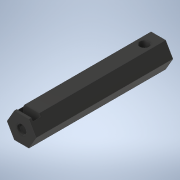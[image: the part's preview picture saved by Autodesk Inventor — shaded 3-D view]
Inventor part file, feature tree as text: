
AUTODESK INVENTOR PART (.ipt)
format: ipt  version: 2020.4 (Build 244396000, 396)  size: 229,376 bytes
history: native  units: mm
features: extrude x11, sketch x11, projected_geometry x6, plane x1, mirror x1
ambient origin geometry x8: Origin, YZ Plane, XZ Plane, XY Plane, X Axis, Y Axis, Z Axis, Center Point
bodies: Solid1 (feature_tree)
feature tree (30):
  extrude  "Extrusion1"  Depth=44.0mm TaperAngle=0.0deg
  extrude  "Extrusion2"  Depth=5.6mm
  extrude  "Extrusion3"  Depth=3.0mm
  plane  "Work Plane1"
  mirror  "Mirror1"
  extrude  "Extrusion4"  TaperAngle=0.0deg  [1 undecoded]
  extrude  "Extrusion5"  TaperAngle=120.0deg  [1 undecoded]
  extrude  "Extrusion6"  Depth=9.5mm TaperAngle=0.0deg
  extrude  "Extrusion8"  Depth=5.6mm
  extrude  "Extrusion9"  Depth=6.0mm TaperAngle=0.0deg
  extrude  "Extrusion10"  TaperAngle=120.0deg  [1 undecoded]
  extrude  "Extrusion11"  Depth=1.9345mm
  extrude  "Extrusion12"  Depth=2.5mm
  sketch  "Sketch1"  dims[d0=4.05mm d1=44.0mm d2=0.0mm]
  sketch  "Sketch2"  dims[d3=2.5mm d4=5.6mm]
  sketch  "Sketch3"  dims[d5=6.0mm d6=0.0mm d7=3.0mm]
  sketch  "Sketch4"  dims[d8=8.0mm d9=0.0mm d10=0.0mm]
  sketch  "Sketch5"  dims[d11=6.0mm d12=120.0deg]
  projected_geometry  "Projected Loop1"
  projected_geometry  "Projected Loop2"
  sketch  "Sketch6"  dims[d13=120.0deg d14=9.5mm d15=0.0mm]
  sketch  "Sketch8"  dims[d16=2.5mm d17=5.6mm]
  sketch  "Sketch9"  dims[d18=6.0mm d19=6.0mm d20=0.0mm]
  projected_geometry  "Projected Loop4"
  sketch  "Sketch10"  dims[d21=120.0deg d22=120.0deg]
  projected_geometry  "Projected Loop5"
  sketch  "Sketch11"  dims[d23=6.0mm d24=0.0mm d25=1.9345mm]
  projected_geometry  "Projected Loop6"
  sketch  "Sketch12"  dims[d32=5.6mm d33=2.5mm d34=6.5mm d35=0.0mm d36=90.0deg d37=3.0mm d38=0.0mm d39=4.5mm d40=8.0mm d41=0.0mm d42=30.0deg d43=150.0deg d44=2.5mm d45=0.0mm d46=5.6mm d47=2.5mm d48=2.05mm d50=5.85mm d51=0.0mm d52=150.0deg d53=30.0deg d54=5.75mm d55=0.0mm]
  projected_geometry  "Projected Loop7"
note: 3 required parameter values undecoded (feature->parameter linkage not recoverable at this tier; creation-order binding heuristic only, values carry confidence <= 0.55)
